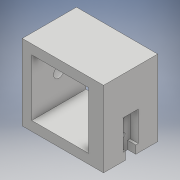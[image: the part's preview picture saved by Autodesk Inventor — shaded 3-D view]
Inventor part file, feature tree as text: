
AUTODESK INVENTOR PART (.ipt)
format: ipt  version: 2017 (Build 210142000, 142)  size: 136,704 bytes
history: native  units: mm
features: extrude x4, sketch x3
ambient origin geometry x8: Origin, YZ Plane, XZ Plane, XY Plane, X Axis, Y Axis, Z Axis, Center Point
bodies: Solid1 (feature_tree)
feature tree (7):
  extrude  "Extrusion1"  Depth=21.0mm
  extrude  "Extrusion2"  Depth=28.0mm
  extrude  "Extrusion3"  Depth=2.5mm
  extrude  "Extrusion4"  Depth=2.5mm
  sketch  "Sketch1"  dims[d0=21.0mm d1=21.0mm]
  sketch  "Sketch4"  dims[d2=28.0mm d3=28.0mm]
  sketch  "Sketch5"  dims[d4=20.0mm d5=0.0mm d6=2.0mm d7=2.8mm d8=2.8mm d10=3.0mm d12=3.0mm d13=0.0mm d14=1.9mm d15=1.9mm d16=6.0mm d17=3.0mm d18=0.0mm d19=3.9mm d20=4.0mm d21=0.0mm d22=2.5mm d24=1.9mm d25=1.9mm]
